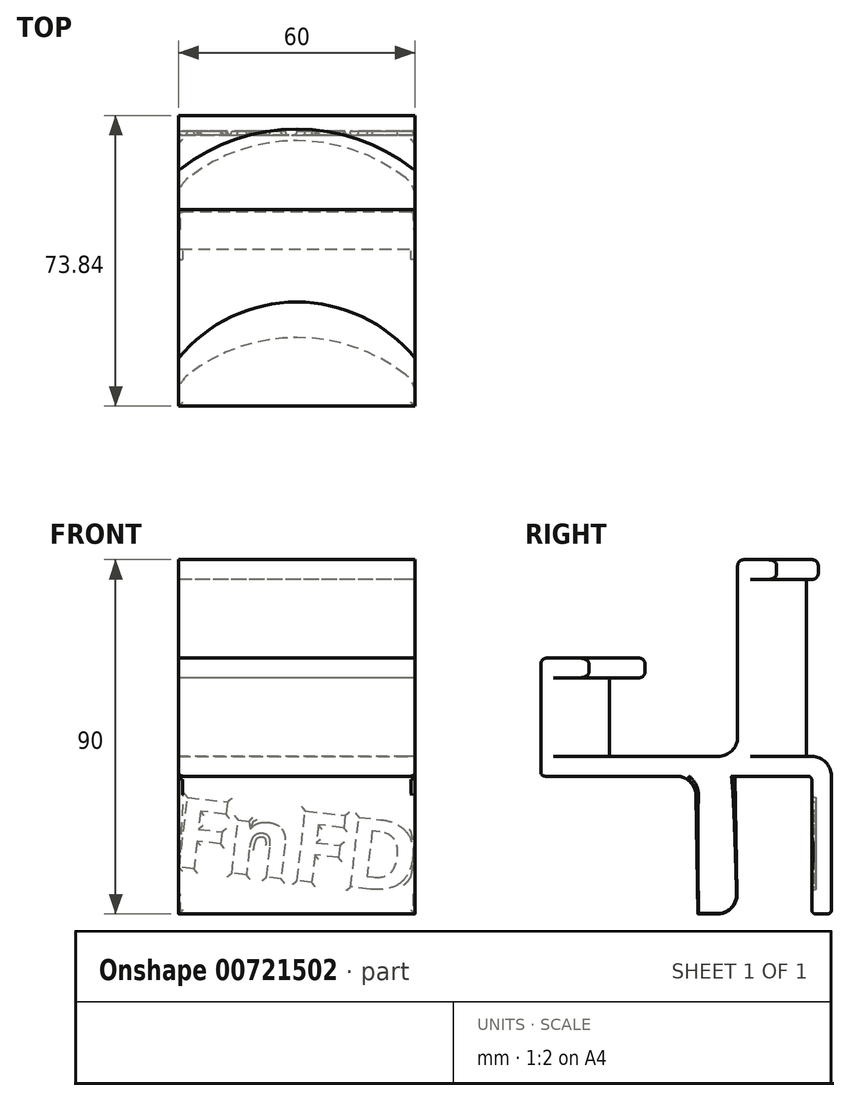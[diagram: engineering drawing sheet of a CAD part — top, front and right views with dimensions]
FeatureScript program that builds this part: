
annotation { "Feature Type Name" : "Feature", "Feature Type Description" : "" }
export const myFeature = defineFeature(function(context is Context, id is Id, definition is map)
    precondition{}
    {
        {
            var Q0;
            Q0=qCreatedBy(makeId("Top.planeOp"),FACE);
            var sketch = newSketch(context, id + "F0", { "sketchPlane" : qUnion([Q0])});
            skArc(sketch, "E0", {"start": v(27.7, 1.93) * mm, "mid": v(0, 11.46) * mm, "end": v(-27.7, 1.93) * mm});
            skLineSegment(sketch, "E1", {"start": v(0, 0) * mm, "end": v(0, -33.54) * mm, "construction": true});
            skLineSegment(sketch, "E2.bottom", {"start": v(-30, 0) * mm, "end": v(30, 0) * mm, "construction": true});
            skLineSegment(sketch, "E2.top", {"start": v(-30, -6) * mm, "end": v(30, -6) * mm});
            skLineSegment(sketch, "E2.left", {"start": v(-30, -2.8) * mm, "end": v(-30, -6) * mm});
            skLineSegment(sketch, "E2.right", {"start": v(30, -2.8) * mm, "end": v(30, -6) * mm});
            skPoint(sketch, "E3.visualSharp", {"position": v(30, 0) * mm});
            skArc(sketch, "E3.filletArc", {"start": v(30, -2.8) * mm, "mid": v(29.4, -0.17) * mm, "end": v(27.7, 1.93) * mm});
            skPoint(sketch, "E4.visualSharp", {"position": v(-30, 0) * mm});
            skArc(sketch, "E4.filletArc", {"start": v(-27.7, 1.93) * mm, "mid": v(-29.4, -0.17) * mm, "end": v(-30, -2.8) * mm});
            skSolve(sketch);
        }
        {
            var Q0;
            Q0=makeQuery(id+"F0.imprint","IMPRINT",FACE,{"disambiguationData":[TD([[makeQuery(id+"F0.imprint","IMPRINT",EDGE,{"derivedFrom":sQuery(id+"F0.wireOp",EDGE,"E0")}),1.0]])]});
            extrude(context, id + "F1", {"entities" : qUnion([Q0]), "depth" : 45 * mm, "offsetDistance" : 25 * mm});
        }
        {
            var Q0;
            Q0=makeQuery(id+"F1.opExtrude","CAP_FACE",FACE,{"disambiguationData":[OSD([sQuery(id+"F0.wireOp",EDGE,"E0"),sQuery(id+"F0.wireOp",EDGE,"E2.top"),sQuery(id+"F0.wireOp",EDGE,"E2.left"),sQuery(id+"F0.wireOp",EDGE,"E2.right"),sQuery(id+"F0.wireOp",EDGE,"E3.filletArc"),sQuery(id+"F0.wireOp",EDGE,"E4.filletArc")])],"isStart":false});
            var sketch = newSketch(context, id + "F2", { "sketchPlane" : qUnion([Q0])});
            skArc(sketch, "E5.0", {"start": v(33, -2.8) * mm, "mid": v(32.09, 1.15) * mm, "end": v(29.54, 4.3) * mm});
            skArc(sketch, "E5.1", {"start": v(-29.54, 4.3) * mm, "mid": v(-32.09, 1.15) * mm, "end": v(-33, -2.8) * mm});
            skLineSegment(sketch, "E5.2", {"start": v(-33, -2.8) * mm, "end": v(-33, -9) * mm});
            skArc(sketch, "E5.3", {"start": v(29.54, 4.3) * mm, "mid": v(0, 14.46) * mm, "end": v(-29.54, 4.3) * mm});
            skLineSegment(sketch, "E5.4", {"start": v(-33, -9) * mm, "end": v(33, -9) * mm});
            skLineSegment(sketch, "E5.5", {"start": v(33, -2.8) * mm, "end": v(33, -9) * mm});
            skLineSegment(sketch, "E6", {"start": v(-30, -6) * mm, "end": v(-33, -6) * mm});
            skPoint(sketch, "E6.endSnap0", {"position": v(-33, -5.9) * mm});
            skLineSegment(sketch, "E7", {"start": v(30, -6) * mm, "end": v(33, -6) * mm});
            skPoint(sketch, "E7.endSnap0", {"position": v(33, -5.9) * mm});
            skSolve(sketch);
        }
        {
            var Q0;
            Q0=makeQuery(id+"F2.imprint","IMPRINT",FACE,{"disambiguationData":[TD([[makeQuery(id+"F2.imprint","IMPRINT",EDGE,{"derivedFrom":sQuery(id+"F2.wireOp",EDGE,"E5.0")}),1.0]])]});
            var Q1;
            Q1=makeQuery(id+"F2.imprint","IMPRINT",FACE,{"disambiguationData":[TD([[makeQuery(id+"F2.imprint","IMPRINT",EDGE,{"derivedFrom":makeQuery(id+"F1.opExtrude","CAP_EDGE",EDGE,{"disambiguationData":[OSD([sQuery(id+"F0.wireOp",EDGE,"E0")])],"isStart":false})}),1.0]])]});
            extrude(context, id + "F3", {"entities" : qUnion([Q0, Q1]), "operationType" : NewBodyOperationType.ADD, "depth" : 5 * mm, "offsetDistance" : 25 * mm});
        }
        {
            var Q0;
            Q0=makeQuery(id+"F1.opExtrude","CAP_EDGE",EDGE,{"disambiguationData":[OSD([sQuery(id+"F0.wireOp",EDGE,"E0")])],"isStart":false});
            var Q1;
            Q1=makeQuery(id+"F3.opExtrude","CAP_EDGE",EDGE,{"disambiguationData":[OSD([sQuery(id+"F2.wireOp",EDGE,"E5.3")])],"isStart":true});
            var Q2;
            Q2=makeQuery(id+"F3.opExtrude","CAP_EDGE",EDGE,{"disambiguationData":[OSD([sQuery(id+"F2.wireOp",EDGE,"E5.3")])],"isStart":false});
            var Q3;
            Q3=makeQuery(id+"F1.opExtrude","CAP_EDGE",EDGE,{"disambiguationData":[OSD([sQuery(id+"F0.wireOp",EDGE,"E4.filletArc")])],"isStart":false});
            var Q4;
            Q4=makeQuery(id+"F3.opExtrude","CAP_EDGE",EDGE,{"disambiguationData":[OSD([sQuery(id+"F2.wireOp",EDGE,"E5.1")])],"isStart":true});
            var Q5;
            Q5=makeQuery(id+"F1.opExtrude","CAP_EDGE",EDGE,{"disambiguationData":[OSD([sQuery(id+"F0.wireOp",EDGE,"E2.left")])],"isStart":false});
            var Q6;
            Q6=makeQuery(id+"F3.opExtrude","CAP_EDGE",EDGE,{"disambiguationData":[OSD([sQuery(id+"F2.wireOp",EDGE,"E5.2")])],"isStart":true});
            var Q7;
            Q7=makeQuery(id+"F3.opExtrude","CAP_EDGE",EDGE,{"disambiguationData":[OSD([sQuery(id+"F2.wireOp",EDGE,"E5.1")])],"isStart":false});
            var Q8;
            Q8=makeQuery(id+"F3.opExtrude","CAP_EDGE",EDGE,{"disambiguationData":[OSD([sQuery(id+"F2.wireOp",EDGE,"E5.2")])],"isStart":false});
            var Q9;
            Q9=makeQuery(id+"F3.opExtrude","CAP_EDGE",EDGE,{"disambiguationData":[OSD([sQuery(id+"F2.wireOp",EDGE,"E5.0")])],"isStart":true});
            var Q10;
            Q10=makeQuery(id+"F3.opExtrude","CAP_EDGE",EDGE,{"disambiguationData":[OSD([sQuery(id+"F2.wireOp",EDGE,"E5.0")])],"isStart":false});
            var Q11;
            Q11=makeQuery(id+"F3.opExtrude","CAP_EDGE",EDGE,{"disambiguationData":[OSD([sQuery(id+"F2.wireOp",EDGE,"E5.5")])],"isStart":true});
            var Q12;
            Q12=makeQuery(id+"F3.opExtrude","CAP_EDGE",EDGE,{"disambiguationData":[OSD([sQuery(id+"F2.wireOp",EDGE,"E5.5")])],"isStart":false});
            var Q13;
            Q13=makeQuery(id+"F1.opExtrude","CAP_EDGE",EDGE,{"disambiguationData":[OSD([sQuery(id+"F0.wireOp",EDGE,"E3.filletArc")])],"isStart":false});
            var Q14;
            Q14=makeQuery(id+"F1.opExtrude","CAP_EDGE",EDGE,{"disambiguationData":[OSD([sQuery(id+"F0.wireOp",EDGE,"E2.right")])],"isStart":false});
            fillet(context, id + "F4", {"entities" : qUnion([Q0, Q1, Q2, Q3, Q4, Q5, Q6, Q7, Q8, Q9, Q10, Q11, Q12, Q13, Q14]), "radius" : 1.5 * mm, "tangentPropagation" : true, "allowEdgeOverflow" : false});
        }
        {
            var Q0;
            Q0=makeQuery(id+"F1.opExtrude","CAP_FACE",FACE,{"disambiguationData":[OSD([sQuery(id+"F0.wireOp",EDGE,"E0"),sQuery(id+"F0.wireOp",EDGE,"E2.top"),sQuery(id+"F0.wireOp",EDGE,"E2.left"),sQuery(id+"F0.wireOp",EDGE,"E2.right"),sQuery(id+"F0.wireOp",EDGE,"E3.filletArc"),sQuery(id+"F0.wireOp",EDGE,"E4.filletArc")])],"isStart":true});
            var sketch = newSketch(context, id + "F5", { "sketchPlane" : qUnion([Q0])});
            skLineSegment(sketch, "E8.bottom", {"start": v(-30, 6) * mm, "end": v(30, 6) * mm});
            skLineSegment(sketch, "E8.top", {"start": v(-30, -17.84) * mm, "end": v(30, -17.84) * mm});
            skLineSegment(sketch, "E8.left", {"start": v(-30, 6) * mm, "end": v(-30, -17.84) * mm});
            skLineSegment(sketch, "E8.right", {"start": v(30, 6) * mm, "end": v(30, -17.84) * mm});
            skLineSegment(sketch, "E9.bottom", {"start": v(-30, 6) * mm, "end": v(30, 6) * mm, "construction": true});
            skLineSegment(sketch, "E9.top", {"start": v(-30, 56) * mm, "end": v(30, 56) * mm});
            skLineSegment(sketch, "E9.left", {"start": v(-30, 6) * mm, "end": v(-30, 56) * mm});
            skLineSegment(sketch, "E9.right", {"start": v(30, 6) * mm, "end": v(30, 56) * mm});
            skSolve(sketch);
        }
        {
            var Q0;
            {var subQ2=sQuery(id+"F5.wireOp",EDGE,"E8.top");Q0=makeQuery(id+"F5.imprint","IMPRINT",FACE,{"disambiguationData":[TD([[makeQuery(id+"F5.imprint","IMPRINT",EDGE,{"derivedFrom":subQ2}),1.0]])]});}
            var Q1;
            {var subQ1=sQuery(id+"F5.wireOp",EDGE,"E8.bottom");Q1=makeQuery(id+"F5.imprint","IMPRINT",FACE,{"disambiguationData":[TD([[makeQuery(id+"F5.imprint","IMPRINT",EDGE,{"derivedFrom":subQ1}),-1.0]])]});}
            var Q2;
            Q2=makeQuery(id+"F5.imprint","IMPRINT",FACE,{"disambiguationData":[TD([[makeQuery(id+"F5.imprint","IMPRINT",EDGE,{"derivedFrom":sQuery(id+"F5.wireOp",EDGE,"E8.bottom")}),1.0]])]});
            extrude(context, id + "F6", {"entities" : qUnion([Q0, Q1, Q2]), "operationType" : NewBodyOperationType.ADD, "depth" : 5 * mm, "offsetDistance" : 25 * mm});
        }
        {
            var Q0;
            Q0=makeQuery(id+"F6.opExtrude","CAP_FACE",FACE,{"disambiguationData":[OSD([sQuery(id+"F5.wireOp",EDGE,"E8.top"),sQuery(id+"F5.wireOp",EDGE,"E8.left"),sQuery(id+"F5.wireOp",EDGE,"E8.right"),sQuery(id+"F5.wireOp",EDGE,"E9.top"),sQuery(id+"F5.wireOp",EDGE,"E9.left"),sQuery(id+"F5.wireOp",EDGE,"E9.right")])],"isStart":false});
            var sketch = newSketch(context, id + "F7", { "sketchPlane" : qUnion([Q0])});
            skLineSegment(sketch, "E10.bottom", {"start": v(-30, -17.84) * mm, "end": v(30, -17.84) * mm});
            skLineSegment(sketch, "E10.top", {"start": v(-30, -12.84) * mm, "end": v(30, -12.84) * mm});
            skLineSegment(sketch, "E10.left", {"start": v(-30, -17.84) * mm, "end": v(-30, -12.84) * mm});
            skLineSegment(sketch, "E10.right", {"start": v(30, -17.84) * mm, "end": v(30, -12.84) * mm});
            skSolve(sketch);
        }
        {
            var Q0;
            Q0=makeQuery(id+"F7.imprint","IMPRINT",FACE,{"disambiguationData":[TD([[makeQuery(id+"F7.imprint","IMPRINT",EDGE,{"derivedFrom":sQuery(id+"F7.wireOp",EDGE,"E10.bottom")}),1.0]])]});
            extrude(context, id + "F8", {"entities" : qUnion([Q0]), "operationType" : NewBodyOperationType.ADD, "depth" : 35 * mm, "offsetDistance" : 25 * mm});
        }
        {
            var Q0;
            Q0=makeQuery(id+"F8.opExtrude","CAP_FACE",FACE,{"disambiguationData":[OSD([sQuery(id+"F7.wireOp",EDGE,"E10.bottom"),sQuery(id+"F7.wireOp",EDGE,"E10.top"),sQuery(id+"F7.wireOp",EDGE,"E10.left"),sQuery(id+"F7.wireOp",EDGE,"E10.right")])],"isStart":false});
            var sketch = newSketch(context, id + "F9", { "sketchPlane" : qUnion([Q0])});
            skLineSegment(sketch, "E11.bottom", {"start": v(-30, -17.84) * mm, "end": v(30, -17.84) * mm});
            skLineSegment(sketch, "E11.top", {"start": v(-30, 12.16) * mm, "end": v(30, 12.16) * mm});
            skLineSegment(sketch, "E11.left", {"start": v(-30, -17.84) * mm, "end": v(-30, 12.16) * mm});
            skLineSegment(sketch, "E11.right", {"start": v(30, -17.84) * mm, "end": v(30, 12.16) * mm});
            skSolve(sketch);
        }
        {
            var Q0;
            Q0=makeQuery(id+"F8.opExtrude","CAP_EDGE",EDGE,{"disambiguationData":[OSD([sQuery(id+"F7.wireOp",EDGE,"E10.top")])],"isStart":true});
            var Q1;
            Q1=makeQuery(id+"F1.opExtrude","CAP_EDGE",EDGE,{"disambiguationData":[OSD([sQuery(id+"F0.wireOp",EDGE,"E2.top")])],"isStart":true});
            var Q2;
            Q2=makeQuery(id+"F6.opExtrude","CAP_EDGE",EDGE,{"disambiguationData":[OSD([sQuery(id+"F5.wireOp",EDGE,"E8.top")])],"isStart":true});
            fillet(context, id + "F10", {"entities" : qUnion([Q0, Q1, Q2]), "radius" : 5 * mm, "tangentPropagation" : true, "allowEdgeOverflow" : false});
        }
        {
            var Q0;
            Q0=makeQuery(id+"F8.opExtrude","SWEPT_FACE",FACE,{"disambiguationData":[OSD([sQuery(id+"F7.wireOp",EDGE,"E10.top")])]});
            var sketch = newSketch(context, id + "F11", { "sketchPlane" : qUnion([Q0])});
            skText(sketch, "E12", { "text": "FnFD", "fontName": "OpenSans-Bold.ttf"});
            const initialGuessF11  = {"E12": [-0.03206, -0.02786, 0.99344, -0.11434, 0.01798]};
            skSetInitialGuess(sketch, initialGuessF11);
            skSolve(sketch);
        }
        {
            var Q0;
            Q0=makeQuery(id+"F11.imprint","IMPRINT",FACE,{"disambiguationData":[TD([[makeQuery(id+"F11.imprint","IMPRINT",EDGE,{"derivedFrom":sQuery(id+"F11.wireOp",EDGE,"E12.sketch_text.stroke-0")}),-1.0]])]});
            var Q1;
            Q1=makeQuery(id+"F11.imprint","IMPRINT",FACE,{"disambiguationData":[TD([[makeQuery(id+"F11.imprint","IMPRINT",EDGE,{"derivedFrom":sQuery(id+"F11.wireOp",EDGE,"E12.sketch_text.stroke-10")}),-1.0]])]});
            var Q2;
            Q2=makeQuery(id+"F11.imprint","IMPRINT",FACE,{"disambiguationData":[TD([[makeQuery(id+"F11.imprint","IMPRINT",EDGE,{"derivedFrom":sQuery(id+"F11.wireOp",EDGE,"E12.sketch_text.stroke-27")}),-1.0]])]});
            var Q3;
            Q3=makeQuery(id+"F11.imprint","IMPRINT",FACE,{"disambiguationData":[TD([[makeQuery(id+"F11.imprint","IMPRINT",EDGE,{"derivedFrom":sQuery(id+"F11.wireOp",EDGE,"E12.sketch_text.stroke-37")}),-1.0]])]});
            var Q4;
            {var subQ6=sQuery(id+"F11.wireOp",EDGE,"E12.sketch_text.stroke-2");Q4=makeQuery(id+"F11.imprint","IMPRINT",FACE,{"disambiguationData":[TD([[makeQuery(id+"F11.imprint","IMPRINT",EDGE,{"derivedFrom":subQ6}),-1.0]])]});}
            extrude(context, id + "F12", {"entities" : qUnion([Q0, Q1, Q2, Q3, Q4]), "operationType" : NewBodyOperationType.REMOVE, "oppositeDirection" : true, "depth" : 1 * mm, "offsetDistance" : 25 * mm});
        }
        {
            var Q0;
            {var subQ0=sQuery(id+"F0.wireOp",EDGE,"E2.top");var subQ1=sQuery(id+"F5.wireOp",EDGE,"E9.top");var subQ2=sQuery(id+"F5.wireOp",EDGE,"E9.right");var subQ3=sQuery(id+"F5.wireOp",EDGE,"E8.right");var subQ4=sQuery(id+"F5.wireOp",EDGE,"E9.left");var subQ5=sQuery(id+"F5.wireOp",EDGE,"E8.left");Q0=makeQuery(id+"F6.boolean.opBoolean","SPLIT",FACE,{"disambiguationData":[TD([makeQuery(id+"F1.opExtrude","SWEPT_FACE",FACE,{"disambiguationData":[OSD([subQ0])]})])],"derivedFrom":makeQuery(id+"F6.opExtrude","CAP_FACE",FACE,{"disambiguationData":[OSD([sQuery(id+"F5.wireOp",EDGE,"E8.top"),subQ5,subQ3,subQ1,subQ4,subQ2])],"isStart":true})});}
            var sketch = newSketch(context, id + "F13", { "sketchPlane" : qUnion([Q0])});
            skArc(sketch, "E13", {"start": v(27.7, -48.07) * mm, "mid": v(0, -38.54) * mm, "end": v(-27.7, -48.07) * mm});
            skLineSegment(sketch, "E14", {"start": v(0, -38.54) * mm, "end": v(0, -83.54) * mm, "construction": true});
            skLineSegment(sketch, "E15.bottom", {"start": v(-30, -50) * mm, "end": v(30, -50) * mm, "construction": true});
            skLineSegment(sketch, "E15.top", {"start": v(-30, -56) * mm, "end": v(30, -56) * mm});
            skLineSegment(sketch, "E15.left", {"start": v(-30, -52.8) * mm, "end": v(-30, -56) * mm});
            skLineSegment(sketch, "E15.right", {"start": v(30, -52.8) * mm, "end": v(30, -56) * mm});
            skPoint(sketch, "E16.visualSharp", {"position": v(30, -50) * mm});
            skArc(sketch, "E16.filletArc", {"start": v(30, -52.8) * mm, "mid": v(29.4, -50.17) * mm, "end": v(27.7, -48.07) * mm});
            skPoint(sketch, "E17.visualSharp", {"position": v(-30, -50) * mm});
            skArc(sketch, "E17.filletArc", {"start": v(-27.7, -48.07) * mm, "mid": v(-29.4, -50.17) * mm, "end": v(-30, -52.8) * mm});
            skSolve(sketch);
        }
        {
            var Q0;
            Q0=makeQuery(id+"F13.imprint","IMPRINT",FACE,{"disambiguationData":[TD([[makeQuery(id+"F13.imprint","IMPRINT",EDGE,{"derivedFrom":sQuery(id+"F13.wireOp",EDGE,"E13")}),1.0]])]});
            extrude(context, id + "F14", {"entities" : qUnion([Q0]), "operationType" : NewBodyOperationType.ADD, "depth" : 20 * mm, "offsetDistance" : 25 * mm});
        }
        {
            var Q0;
            Q0=makeQuery(id+"F14.opExtrude","CAP_FACE",FACE,{"disambiguationData":[OSD([sQuery(id+"F13.wireOp",EDGE,"E13"),sQuery(id+"F13.wireOp",EDGE,"E15.top"),sQuery(id+"F13.wireOp",EDGE,"E15.left"),sQuery(id+"F13.wireOp",EDGE,"E15.right"),sQuery(id+"F13.wireOp",EDGE,"E16.filletArc"),sQuery(id+"F13.wireOp",EDGE,"E17.filletArc")])],"isStart":false});
            var sketch = newSketch(context, id + "F15", { "sketchPlane" : qUnion([Q0])});
            skLineSegment(sketch, "E18.2", {"start": v(-33, -48) * mm, "end": v(-33, -56) * mm});
            skLineSegment(sketch, "E18.4", {"start": v(-33, -56) * mm, "end": v(33, -56) * mm});
            skLineSegment(sketch, "E18.5", {"start": v(33, -48) * mm, "end": v(33, -56) * mm});
            skLineSegment(sketch, "E19", {"start": v(-30, -53) * mm, "end": v(-33, -53) * mm});
            skPoint(sketch, "E19.endSnap0", {"position": v(-33, -52) * mm});
            skLineSegment(sketch, "E20", {"start": v(30, -52.56) * mm, "end": v(33, -52.56) * mm});
            skPoint(sketch, "E20.endSnap0", {"position": v(33, -52) * mm});
            skLineSegment(sketch, "E21", {"start": v(0, -56) * mm, "end": v(0, -52.75) * mm, "construction": true});
            skLineSegment(sketch, "E22", {"start": v(0, -56) * mm, "end": v(0, -60.11) * mm, "construction": true});
            skArc(sketch, "E23", {"start": v(33, -48) * mm, "mid": v(0, -29.54) * mm, "end": v(-33, -48) * mm});
            skSolve(sketch);
        }
        {
            var Q0;
            {var subQ3=sQuery(id+"F15.wireOp",EDGE,"E18.0");Q0=makeQuery(id+"F15.imprint","IMPRINT",FACE,{"disambiguationData":[TD([[makeQuery(id+"F15.imprint","IMPRINT",EDGE,{"derivedFrom":subQ3}),1.0]])]});}
            var Q1;
            Q1=makeQuery(id+"F15.imprint","IMPRINT",FACE,{"disambiguationData":[TD([[makeQuery(id+"F15.imprint","IMPRINT",EDGE,{"derivedFrom":makeQuery(id+"F14.opExtrude","CAP_EDGE",EDGE,{"disambiguationData":[OSD([sQuery(id+"F13.wireOp",EDGE,"E13")])],"isStart":false})}),1.0]])]});
            var Q2;
            {var subQ3=sQuery(id+"F15.wireOp",EDGE,"E19");Q2=makeQuery(id+"F15.imprint","IMPRINT",FACE,{"disambiguationData":[TD([[makeQuery(id+"F15.imprint","IMPRINT",EDGE,{"derivedFrom":subQ3}),1.0]])]});}
            var Q3;
            {var subQ5=sQuery(id+"F15.wireOp",EDGE,"E20");Q3=makeQuery(id+"F15.imprint","IMPRINT",FACE,{"disambiguationData":[TD([[makeQuery(id+"F15.imprint","IMPRINT",EDGE,{"derivedFrom":subQ5}),-1.0]])]});}
            var Q4;
            {var subQ3=sQuery(id+"F15.wireOp",EDGE,"E19");Q4=makeQuery(id+"F15.imprint","IMPRINT",FACE,{"disambiguationData":[TD([[makeQuery(id+"F15.imprint","IMPRINT",EDGE,{"derivedFrom":subQ3}),-1.0]])]});}
            extrude(context, id + "F16", {"entities" : qUnion([Q0, Q1, Q2, Q3, Q4]), "operationType" : NewBodyOperationType.ADD, "depth" : 5 * mm, "offsetDistance" : 25 * mm});
        }
        {
            var Q0;
            Q0=makeQuery(id+"F6.opExtrude","CAP_FACE",FACE,{"disambiguationData":[OSD([sQuery(id+"F5.wireOp",EDGE,"E8.top"),sQuery(id+"F5.wireOp",EDGE,"E8.left"),sQuery(id+"F5.wireOp",EDGE,"E8.right"),sQuery(id+"F5.wireOp",EDGE,"E9.top"),sQuery(id+"F5.wireOp",EDGE,"E9.left"),sQuery(id+"F5.wireOp",EDGE,"E9.right")])],"isStart":false});
            var sketch = newSketch(context, id + "F17", { "sketchPlane" : qUnion([Q0])});
            skLineSegment(sketch, "E24.bottom", {"start": v(-30, 16.66) * mm, "end": v(30, 16.66) * mm});
            skLineSegment(sketch, "E24.top", {"start": v(-30, 6.66) * mm, "end": v(30, 6.66) * mm});
            skLineSegment(sketch, "E24.left", {"start": v(-30, 16.66) * mm, "end": v(-30, 6.66) * mm});
            skLineSegment(sketch, "E24.right", {"start": v(30, 16.66) * mm, "end": v(30, 6.66) * mm});
            skSolve(sketch);
        }
        {
            var Q0;
            Q0=makeQuery(id+"F17.imprint","IMPRINT",FACE,{"disambiguationData":[TD([[makeQuery(id+"F17.imprint","IMPRINT",EDGE,{"derivedFrom":sQuery(id+"F17.wireOp",EDGE,"E24.bottom")}),-1.0]])]});
            var Q1;
            Q1=makeQuery(id+"F8.opExtrude","CAP_FACE",FACE,{"disambiguationData":[OSD([sQuery(id+"F7.wireOp",EDGE,"E10.bottom"),sQuery(id+"F7.wireOp",EDGE,"E10.top"),sQuery(id+"F7.wireOp",EDGE,"E10.left"),sQuery(id+"F7.wireOp",EDGE,"E10.right")])],"isStart":false});
            extrude(context, id + "F18", {"entities" : qUnion([Q0]), "operationType" : NewBodyOperationType.ADD, "endBound" : BoundingType.UP_TO_SURFACE, "depth" : 25 * mm, "endBoundEntityFace" : qUnion([Q1]), "offsetDistance" : 25 * mm, "hasDraft" : true, "draftAngle" : 1 * degree});
        }
        {
            var Q0;
            {var subQ0=sQuery(id+"F5.wireOp",EDGE,"E9.top");var subQ1=sQuery(id+"F5.wireOp",EDGE,"E9.left");var subQ2=sQuery(id+"F5.wireOp",EDGE,"E8.left");var subQ3=sQuery(id+"F5.wireOp",EDGE,"E9.right");var subQ4=sQuery(id+"F5.wireOp",EDGE,"E8.right");Q0=makeQuery(id+"F18.boolean.opBoolean","SPLIT",FACE,{"disambiguationData":[TD([makeQuery(id+"F6.opExtrude","SWEPT_FACE",FACE,{"disambiguationData":[OSD([subQ0])]})])],"derivedFrom":makeQuery(id+"F6.opExtrude","CAP_FACE",FACE,{"disambiguationData":[OSD([sQuery(id+"F5.wireOp",EDGE,"E8.top"),subQ2,subQ4,subQ0,subQ1,subQ3])],"isStart":false})});}
            extrude(context, id + "F19", {"entities" : qUnion([Q0]), "operationType" : NewBodyOperationType.REMOVE, "depth" : 50 * mm, "offsetDistance" : 25 * mm, "hasDraft" : true, "draftAngle" : 1 * degree});
        }
        {
            var Q0;
            Q0=makeQuery(id+"F18.opExtrude","CAP_EDGE",EDGE,{"disambiguationData":[OSD([sQuery(id+"F17.wireOp",EDGE,"E24.top")])],"isStart":true});
            var Q1;
            {var subQ0=sQuery(id+"F17.wireOp",EDGE,"E24.bottom");Q1=makeQuery(id+"F19.boolean.opBoolean","MERGE",EDGE,{"derivedFrom":[makeQuery(id+"F18.opExtrude","CAP_EDGE",EDGE,{"disambiguationData":[OSD([subQ0])],"isStart":true})],"fromTools":[makeQuery(id+"F19.opExtrude","CAP_EDGE",EDGE,{"disambiguationData":[OSD([subQ0])],"isStart":true})]});}
            var Q2;
            Q2=makeQuery(id+"F18.opExtrude","CAP_EDGE",EDGE,{"disambiguationData":[OSD([sQuery(id+"F17.wireOp",EDGE,"E24.top")])],"isStart":false});
            var Q3;
            Q3=makeQuery(id+"F18.opExtrude","TWEAK_EDGE",EDGE,{"derivedFrom":[makeQuery(id+"F8.opExtrude","CAP_FACE",FACE,{"disambiguationData":[OSD([sQuery(id+"F7.wireOp",EDGE,"E10.bottom"),sQuery(id+"F7.wireOp",EDGE,"E10.top"),sQuery(id+"F7.wireOp",EDGE,"E10.left"),sQuery(id+"F7.wireOp",EDGE,"E10.right")])],"isStart":false}),makeQuery(id+"F17.imprint","IMPRINT",EDGE,{"derivedFrom":sQuery(id+"F17.wireOp",EDGE,"E24.bottom")})]});
            fillet(context, id + "F20", {"entities" : qUnion([Q0, Q1, Q2, Q3]), "radius" : 5 * mm, "tangentPropagation" : true, "allowEdgeOverflow" : false});
        }
        {
            var Q0;
            Q0=makeQuery(id+"F14.opExtrude","CAP_EDGE",EDGE,{"disambiguationData":[OSD([sQuery(id+"F13.wireOp",EDGE,"E13")])],"isStart":true});
            var Q1;
            Q1=makeQuery(id+"F16.opExtrude","CAP_EDGE",EDGE,{"disambiguationData":[OSD([sQuery(id+"F15.wireOp",EDGE,"E18.3")])],"isStart":false});
            var Q2;
            Q2=makeQuery(id+"F16.opExtrude","CAP_EDGE",EDGE,{"disambiguationData":[OSD([sQuery(id+"F15.wireOp",EDGE,"E18.3")])],"isStart":true});
            var Q3;
            Q3=makeQuery(id+"F1.opExtrude","CAP_EDGE",EDGE,{"disambiguationData":[OSD([sQuery(id+"F0.wireOp",EDGE,"E0")])],"isStart":true});
            var Q4;
            Q4=makeQuery(id+"F14.opExtrude","CAP_EDGE",EDGE,{"disambiguationData":[OSD([sQuery(id+"F13.wireOp",EDGE,"E13")])],"isStart":false});
            var Q5;
            Q5=makeQuery(id+"F3.opExtrude","CAP_EDGE",EDGE,{"disambiguationData":[OSD([sQuery(id+"F0.wireOp",EDGE,"E2.top"),sQuery(id+"F2.wireOp",EDGE,"E6"),sQuery(id+"F2.wireOp",EDGE,"E7")])],"isStart":false});
            var Q6;
            Q6=makeQuery(id+"F16.opExtrude","CAP_EDGE",EDGE,{"disambiguationData":[OSD([sQuery(id+"F15.wireOp",EDGE,"E18.4")])],"isStart":false});
            var Q7;
            Q7=makeQuery(id+"F16.opExtrude","CAP_EDGE",EDGE,{"disambiguationData":[OSD([sQuery(id+"F15.wireOp",EDGE,"E23")])],"isStart":true});
            var Q8;
            Q8=makeQuery(id+"F16.opExtrude","CAP_EDGE",EDGE,{"disambiguationData":[OSD([sQuery(id+"F15.wireOp",EDGE,"E23")])],"isStart":false});
            fillet(context, id + "F21", {"entities" : qUnion([Q0, Q1, Q2, Q3, Q4, Q5, Q6, Q7, Q8]), "radius" : 1.5 * mm, "tangentPropagation" : true, "allowEdgeOverflow" : false});
        }
        {
            var Q0;
            {var subQ0=sQuery(id+"F7.wireOp",EDGE,"E10.top");Q0=makeQuery(id+"F12.boolean.opBoolean","SPLIT",FACE,{"disambiguationData":[TD([makeQuery(id+"F1.opExtrude","SWEPT_FACE",FACE,{"disambiguationData":[OSD([sQuery(id+"F0.wireOp",EDGE,"E2.left")])]})])],"derivedFrom":makeQuery(id+"F8.opExtrude","SWEPT_FACE",FACE,{"disambiguationData":[OSD([subQ0])]})});}
            var Q1;
            Q1=makeQuery(id+"F6.opExtrude","CAP_EDGE",EDGE,{"disambiguationData":[OSD([sQuery(id+"F5.wireOp",EDGE,"E9.top")])],"isStart":false});
            var Q2;
            {var subQ0=sQuery(id+"F5.wireOp",EDGE,"E9.top");var subQ1=sQuery(id+"F5.wireOp",EDGE,"E9.left");var subQ2=sQuery(id+"F5.wireOp",EDGE,"E8.left");Q2=makeQuery(id+"F18.boolean.opBoolean","SPLIT",EDGE,{"disambiguationData":[TD([makeQuery(id+"F6.opExtrude","SWEPT_FACE",FACE,{"disambiguationData":[OSD([subQ0])]})])],"derivedFrom":makeQuery(id+"F6.opExtrude","CAP_EDGE",EDGE,{"disambiguationData":[OSD([subQ2,subQ1])],"isStart":false})});}
            var Q3;
            Q3=makeQuery(id+"F18.opExtrude","SWEPT_EDGE",EDGE,{"disambiguationData":[OSD([sQuery(id+"F5.wireOp",EDGE,"E8.left"),sQuery(id+"F5.wireOp",EDGE,"E9.left"),sQuery(id+"F17.wireOp",EDGE,"E24.top"),sQuery(id+"F17.wireOp",EDGE,"E24.left")])]});
            var Q4;
            Q4=makeQuery(id+"F18.opExtrude","SWEPT_EDGE",EDGE,{"disambiguationData":[OSD([sQuery(id+"F5.wireOp",EDGE,"E8.right"),sQuery(id+"F5.wireOp",EDGE,"E9.right"),sQuery(id+"F17.wireOp",EDGE,"E24.top"),sQuery(id+"F17.wireOp",EDGE,"E24.right")])]});
            var Q5;
            {var subQ0=sQuery(id+"F5.wireOp",EDGE,"E9.top");var subQ1=sQuery(id+"F5.wireOp",EDGE,"E9.right");var subQ2=sQuery(id+"F5.wireOp",EDGE,"E8.right");Q5=makeQuery(id+"F18.boolean.opBoolean","SPLIT",EDGE,{"disambiguationData":[TD([makeQuery(id+"F6.opExtrude","SWEPT_FACE",FACE,{"disambiguationData":[OSD([subQ0])]})])],"derivedFrom":makeQuery(id+"F6.opExtrude","CAP_EDGE",EDGE,{"disambiguationData":[OSD([subQ2,subQ1])],"isStart":false})});}
            var Q6;
            Q6=makeQuery(id+"F8.opExtrude","CAP_EDGE",EDGE,{"disambiguationData":[OSD([sQuery(id+"F7.wireOp",EDGE,"E10.bottom")])],"isStart":false});
            var Q7;
            Q7=makeQuery(id+"F19.boolean.opBoolean","COPY",EDGE,{"derivedFrom":makeQuery(id+"F19.opExtrude","SWEPT_EDGE",EDGE,{"disambiguationData":[OSD([sQuery(id+"F5.wireOp",EDGE,"E8.right"),sQuery(id+"F5.wireOp",EDGE,"E9.right"),sQuery(id+"F17.wireOp",EDGE,"E24.bottom"),sQuery(id+"F17.wireOp",EDGE,"E24.right")])]})});
            var Q8;
            Q8=makeQuery(id+"F19.boolean.opBoolean","COPY",EDGE,{"derivedFrom":makeQuery(id+"F19.opExtrude","SWEPT_EDGE",EDGE,{"disambiguationData":[OSD([sQuery(id+"F5.wireOp",EDGE,"E8.left"),sQuery(id+"F5.wireOp",EDGE,"E9.left"),sQuery(id+"F17.wireOp",EDGE,"E24.bottom"),sQuery(id+"F17.wireOp",EDGE,"E24.left")])]})});
            fillet(context, id + "F22", {"entities" : qUnion([Q0, Q1, Q2, Q3, Q4, Q5, Q6, Q7, Q8]), "radius" : 1 * mm, "tangentPropagation" : true, "allowEdgeOverflow" : false});
        }
        {
            var Q0;
            {var subQ0=sQuery(id+"F9.wireOp",EDGE,"E11.bottom");Q0=makeQuery(id+"F9.imprint","IMPRINT",FACE,{"disambiguationData":[TD([[makeQuery(id+"F9.imprint","IMPRINT",EDGE,{"derivedFrom":subQ0}),1.0]])]});}
            var sketch = newSketch(context, id + "F23", { "sketchPlane" : qUnion([Q0])});
            skLineSegment(sketch, "E25.top", {"start": v(-30, -18.33) * mm, "end": v(30, -18.33) * mm});
            skLineSegment(sketch, "E25.left", {"start": v(-30, 31.6) * mm, "end": v(-30, -18.33) * mm});
            skLineSegment(sketch, "E25.right", {"start": v(30, 31.6) * mm, "end": v(30, -18.33) * mm});
            skLineSegment(sketch, "E26.0", {"start": v(-35, 87.47) * mm, "end": v(-35, -23.33) * mm});
            skLineSegment(sketch, "E26.1", {"start": v(-35, 87.47) * mm, "end": v(35, 87.47) * mm});
            skLineSegment(sketch, "E26.2", {"start": v(35, 87.47) * mm, "end": v(35, -23.33) * mm});
            skLineSegment(sketch, "E26.3", {"start": v(-35, -23.33) * mm, "end": v(35, -23.33) * mm});
            skLineSegment(sketch, "E27", {"start": v(-30, 31.6) * mm, "end": v(-30, 60.9) * mm});
            skLineSegment(sketch, "E28", {"start": v(-30, 60.9) * mm, "end": v(30, 60.9) * mm});
            skLineSegment(sketch, "E29", {"start": v(30, 60.9) * mm, "end": v(30, 31.6) * mm});
            skSolve(sketch);
        }
        {
            var Q0;
            {var subQ0=sQuery(id+"F9.wireOp",EDGE,"E11.top");Q0=makeQuery(id+"F9.imprint","IMPRINT",FACE,{"disambiguationData":[TD([[makeQuery(id+"F9.imprint","IMPRINT",EDGE,{"derivedFrom":subQ0}),-1.0]])]});}
            var Q1;
            {var subQ0=sQuery(id+"F9.wireOp",EDGE,"E11.bottom");Q1=makeQuery(id+"F9.imprint","IMPRINT",FACE,{"disambiguationData":[TD([[makeQuery(id+"F9.imprint","IMPRINT",EDGE,{"derivedFrom":subQ0}),1.0]])]});}
            var Q2;
            {var subQ2=sQuery(id+"F23.wireOp",EDGE,"E27");Q2=makeQuery(id+"F23.imprint","IMPRINT",FACE,{"disambiguationData":[TD([[makeQuery(id+"F23.imprint","IMPRINT",EDGE,{"derivedFrom":subQ2}),-1.0]])]});}
            var Q3;
            {var subQ0=sQuery(id+"F23.wireOp",EDGE,"E25.top");Q3=makeQuery(id+"F23.imprint","IMPRINT",FACE,{"disambiguationData":[TD([[makeQuery(id+"F23.imprint","IMPRINT",EDGE,{"derivedFrom":subQ0}),1.0]])]});}
            extrude(context, id + "F24", {"entities" : qUnion([Q0, Q1, Q2, Q3]), "operationType" : NewBodyOperationType.INTERSECT, "oppositeDirection" : true, "depth" : 126.3 * mm, "offsetDistance" : 25 * mm});
        }
    });
